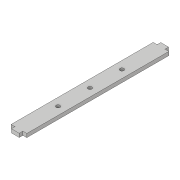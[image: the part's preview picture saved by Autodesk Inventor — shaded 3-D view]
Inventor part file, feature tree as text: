
AUTODESK INVENTOR PART (.ipt)
format: ipt  version: 2017 (Build 210142000, 142)  size: 105,984 bytes
history: native  units: in
note: dims shown in document units (in); Inventor stores cm internally (conversion verified against a paired STEP export)
features: extrude x3, sketch x3
ambient origin geometry x8: Origin, YZ Plane, XZ Plane, XY Plane, X Axis, Y Axis, Z Axis, Center Point
bodies: Solid1 (feature_tree)
feature tree (6):
  extrude  "Extrusion1"  Depth=0.5in
  extrude  "Extrusion2"  Depth=0.125in
  extrude  "Extrusion3"  Depth=0.115in
  sketch  "Sketch1"  dims[d0=4.54in d1=0.5in]
  sketch  "Sketch2"  dims[d2=0.25in d3=0.125in]
  sketch  "Sketch3"  dims[d4=0.115in d5=0.115in d6=0.125in d7=0.115in d8=0.0in d9=0.125in d10=0.125in d11=0.25in d12=0.25in d13=1.25in d14=1.25in d15=0.115in d16=0.0in d17=0.125in d18=0.25in d19=2.27in d20=0.115in d21=0.0in]
